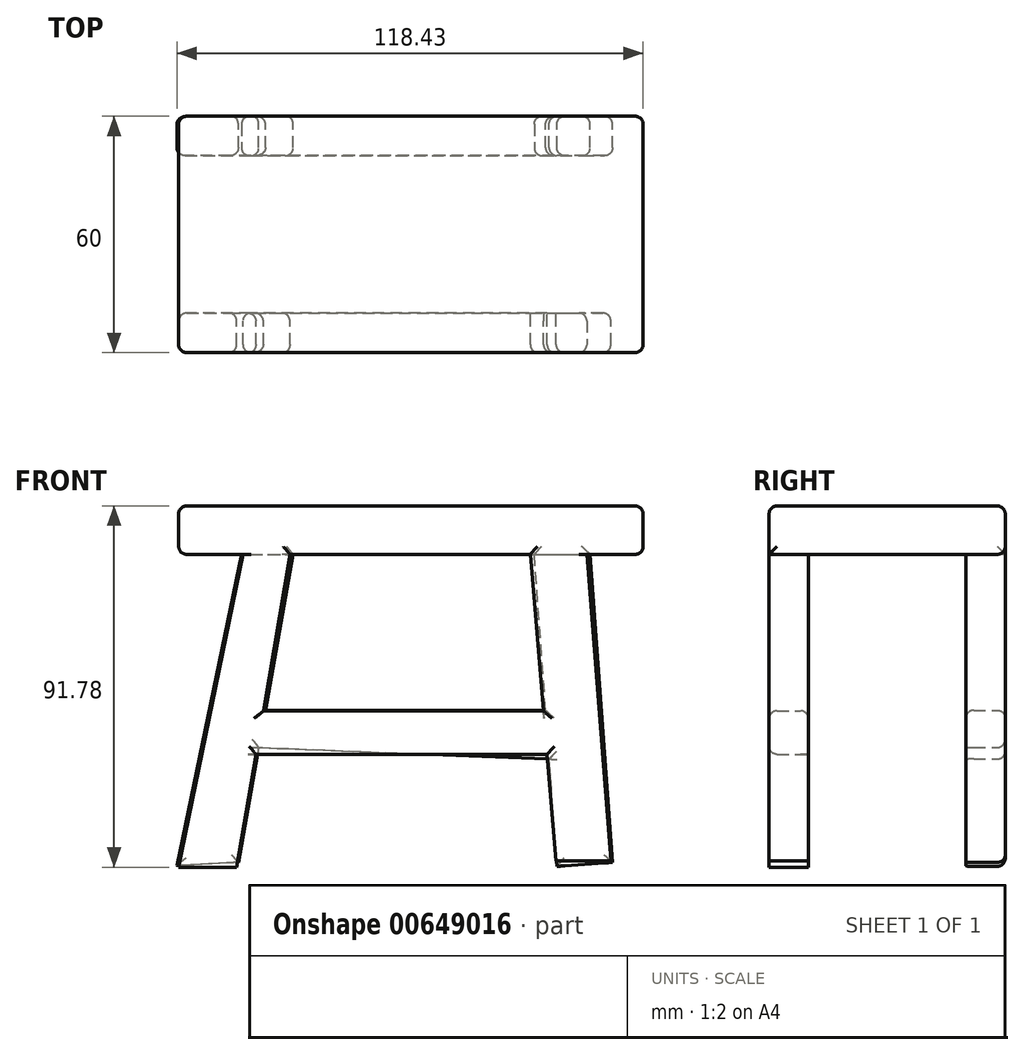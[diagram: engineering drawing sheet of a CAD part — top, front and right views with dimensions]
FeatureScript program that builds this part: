
annotation { "Feature Type Name" : "Feature", "Feature Type Description" : "" }
export const myFeature = defineFeature(function(context is Context, id is Id, definition is map)
    precondition{}
    {
        {
            var Q0;
            Q0=qCreatedBy(makeId("Front.planeOp"),FACE);
            var sketch = newSketch(context, id + "F0", { "sketchPlane" : qUnion([Q0])});
            skLineSegment(sketch, "E0.bottom", {"start": v(-57.16, 35.65) * mm, "end": v(60.84, 35.65) * mm});
            skLineSegment(sketch, "E0.top", {"start": v(-57.16, 23.35) * mm, "end": v(60.84, 23.35) * mm});
            skLineSegment(sketch, "E0.left", {"start": v(-57.16, 35.65) * mm, "end": v(-57.16, 23.35) * mm});
            skLineSegment(sketch, "E0.right", {"start": v(60.84, 35.65) * mm, "end": v(60.84, 23.35) * mm});
            skSolve(sketch);
        }
        {
            var Q0;
            Q0 = qSketchRegion(id + "F0", true);
            extrude(context, id + "F1", {"entities" : qUnion([Q0]), "depth" : 60 * mm, "offsetDistance" : 25 * mm});
        }
        {
            var Q0;
            Q0=qCreatedBy(makeId("Front.planeOp"),FACE);
            cPlane(context, id + "F2", {"entities" : qUnion([Q0]), "cplaneType" : CPlaneType.OFFSET, "offset" : 50 * mm, "width" : 150 * mm, "height" : 150 * mm});
        }
        {
            var Q0;
            Q0=qCreatedBy(id+"F2.planeOp",FACE);
            var sketch = newSketch(context, id + "F3", { "sketchPlane" : qUnion([Q0])});
            skLineSegment(sketch, "E1", {"start": v(-40.77, 23.76) * mm, "end": v(-57.16, -56.13) * mm});
            skLineSegment(sketch, "E2", {"start": v(-57.16, -56.13) * mm, "end": v(-42.4, -56.13) * mm});
            skLineSegment(sketch, "E3", {"start": v(-42.4, -56.13) * mm, "end": v(-28.88, 23.35) * mm});
            skLineSegment(sketch, "E4", {"start": v(-28.88, 23.35) * mm, "end": v(-40.77, 23.76) * mm});
            skLineSegment(sketch, "E5", {"start": v(32.16, 23.35) * mm, "end": v(38.72, -54.5) * mm});
            skLineSegment(sketch, "E6", {"start": v(38.72, -54.5) * mm, "end": v(52.65, -54.5) * mm});
            skLineSegment(sketch, "E7", {"start": v(52.65, -54.5) * mm, "end": v(46.5, 23.76) * mm});
            skLineSegment(sketch, "E8", {"start": v(46.5, 23.76) * mm, "end": v(32.16, 23.35) * mm});
            skLineSegment(sketch, "E9", {"start": v(-35.65, -16.39) * mm, "end": v(35.5, -16.39) * mm});
            skLineSegment(sketch, "E10", {"start": v(35.5, -16.39) * mm, "end": v(36.44, -27.45) * mm});
            skLineSegment(sketch, "E11", {"start": v(36.44, -27.45) * mm, "end": v(-37.53, -27.45) * mm});
            skLineSegment(sketch, "E12", {"start": v(-37.53, -27.45) * mm, "end": v(-35.65, -16.39) * mm});
            skSolve(sketch);
        }
        {
            var Q0;
            Q0 = qSketchRegion(id + "F3", true);
            extrude(context, id + "F4", {"entities" : qUnion([Q0]), "operationType" : NewBodyOperationType.ADD, "depth" : 10 * mm, "offsetDistance" : 25 * mm});
        }
        {
            var Q0;
            Q0=qCreatedBy(makeId("Front.planeOp"),FACE);
            var sketch = newSketch(context, id + "F5", { "sketchPlane" : qUnion([Q0])});
            skLineSegment(sketch, "E13", {"start": v(47.32, 24.17) * mm, "end": v(53.06, -54.9) * mm});
            skLineSegment(sketch, "E14", {"start": v(53.06, -54.9) * mm, "end": v(38.94, -55.93) * mm});
            skLineSegment(sketch, "E15", {"start": v(38.94, -55.93) * mm, "end": v(33.18, 23.43) * mm});
            skLineSegment(sketch, "E16", {"start": v(33.18, 23.43) * mm, "end": v(47.32, 24.17) * mm});
            skLineSegment(sketch, "E17", {"start": v(-28.07, 23.43) * mm, "end": v(-42, -54.9) * mm});
            skLineSegment(sketch, "E18", {"start": v(-42, -54.9) * mm, "end": v(-57.59, -55.72) * mm});
            skLineSegment(sketch, "E19", {"start": v(-57.59, -55.72) * mm, "end": v(-41.18, 23.43) * mm});
            skLineSegment(sketch, "E20", {"start": v(-41.18, 23.43) * mm, "end": v(-28.07, 23.43) * mm});
            skLineSegment(sketch, "E21", {"start": v(36.06, -16.25) * mm, "end": v(-35.12, -16.25) * mm});
            skLineSegment(sketch, "E22", {"start": v(-35.12, -16.25) * mm, "end": v(-36.8, -25.72) * mm});
            skLineSegment(sketch, "E23", {"start": v(36.75, -25.72) * mm, "end": v(36.06, -16.25) * mm});
            skLineSegment(sketch, "E24", {"start": v(-36.8, -25.72) * mm, "end": v(36.96, -28.66) * mm});
            skSolve(sketch);
        }
        {
            var Q0;
            Q0 = qSketchRegion(id + "F5", true);
            extrude(context, id + "F6", {"entities" : qUnion([Q0]), "operationType" : NewBodyOperationType.ADD, "depth" : 10 * mm, "offsetDistance" : 25 * mm});
        }
        {
            var Q0;
            Q0=qCreatedBy(makeId("Right.planeOp"),FACE);
            var sketch = newSketch(context, id + "F7", { "sketchPlane" : qUnion([Q0])});
            skLineSegment(sketch, "E25.bottom", {"start": v(-49.78, 23.35) * mm, "end": v(-10.45, 23.35) * mm});
            skLineSegment(sketch, "E25.top", {"start": v(-49.78, -67.6) * mm, "end": v(-10.45, -67.6) * mm});
            skLineSegment(sketch, "E25.left", {"start": v(-49.78, 23.35) * mm, "end": v(-49.78, -67.6) * mm});
            skLineSegment(sketch, "E25.right", {"start": v(-10.45, 23.35) * mm, "end": v(-10.45, -67.6) * mm});
            skSolve(sketch);
        }
        {
            var Q0;
            Q0 = qSketchRegion(id + "F7", true);
            extrude(context, id + "F8", {"entities" : qUnion([Q0]), "operationType" : NewBodyOperationType.REMOVE, "endBound" : BoundingType.THROUGH_ALL, "oppositeDirection" : true, "depth" : 100 * mm, "offsetDistance" : 25 * mm, "hasSecondDirection" : true, "secondDirectionOppositeDirection" : false, "secondDirectionDepth" : 100 * mm});
        }
        {
            var Q0;
            Q0=makeQuery(id+"F1.opExtrude","CAP_EDGE",EDGE,{"disambiguationData":[OSD([sQuery(id+"F0.wireOp",EDGE,"E0.bottom")])],"isStart":false});
            var Q1;
            {var subQ0=sQuery(id+"F3.wireOp",EDGE,"E4");var subQ1=sQuery(id+"F3.wireOp",EDGE,"E3");var subQ5=sQuery(id+"F0.wireOp",EDGE,"E0.top");Q1=makeQuery(id+"F4.boolean.opBoolean","SPLIT",EDGE,{"disambiguationData":[TD([makeQuery(id+"F4.opExtrude","SWEPT_FACE",FACE,{"disambiguationData":[OSD([subQ1]),TDD([makeQuery(id+"F3.imprint","IMPRINT",EDGE,{"disambiguationData":[TD([[makeQuery(id+"F3.imprint","INTERSECT",VERTEX,{"derivedFrom":[subQ1,subQ0]}),1.0]])],"derivedFrom":subQ1})])]})])],"derivedFrom":makeQuery(id+"F1.opExtrude","CAP_EDGE",EDGE,{"disambiguationData":[OSD([subQ5])],"isStart":false})});}
            var Q2;
            {var subQ0=sQuery(id+"F3.wireOp",EDGE,"E3");Q2=makeQuery(id+"F4.opExtrude","CAP_EDGE",EDGE,{"disambiguationData":[OSD([subQ0]),TDD([makeQuery(id+"F3.imprint","IMPRINT",EDGE,{"disambiguationData":[TD([[makeQuery(id+"F3.imprint","INTERSECT",VERTEX,{"derivedFrom":[subQ0,sQuery(id+"F3.wireOp",EDGE,"E4")]}),1.0]])],"derivedFrom":subQ0})])],"isStart":false});}
            var Q3;
            {var subQ0=sQuery(id+"F3.wireOp",EDGE,"E5");Q3=makeQuery(id+"F4.opExtrude","CAP_EDGE",EDGE,{"disambiguationData":[OSD([subQ0]),TDD([makeQuery(id+"F3.imprint","IMPRINT",EDGE,{"disambiguationData":[TD([[makeQuery(id+"F3.imprint","INTERSECT",VERTEX,{"derivedFrom":[subQ0,sQuery(id+"F3.wireOp",EDGE,"E8")]}),-1.0]])],"derivedFrom":subQ0})])],"isStart":false});}
            var Q4;
            Q4=makeQuery(id+"F4.opExtrude","CAP_EDGE",EDGE,{"disambiguationData":[OSD([sQuery(id+"F3.wireOp",EDGE,"E9")])],"isStart":false});
            var Q5;
            Q5=makeQuery(id+"F4.opExtrude","CAP_EDGE",EDGE,{"disambiguationData":[OSD([sQuery(id+"F3.wireOp",EDGE,"E11")])],"isStart":false});
            var Q6;
            {var subQ0=sQuery(id+"F3.wireOp",EDGE,"E5");Q6=makeQuery(id+"F4.opExtrude","CAP_EDGE",EDGE,{"disambiguationData":[OSD([subQ0]),TDD([makeQuery(id+"F3.imprint","IMPRINT",EDGE,{"disambiguationData":[TD([[makeQuery(id+"F3.imprint","INTERSECT",VERTEX,{"derivedFrom":[subQ0,sQuery(id+"F3.wireOp",EDGE,"E6")]}),1.0]])],"derivedFrom":subQ0})])],"isStart":false});}
            var Q7;
            Q7=makeQuery(id+"F4.opExtrude","CAP_EDGE",EDGE,{"disambiguationData":[OSD([sQuery(id+"F3.wireOp",EDGE,"E7")])],"isStart":false});
            var Q8;
            Q8=makeQuery(id+"F4.opExtrude","CAP_EDGE",EDGE,{"disambiguationData":[OSD([sQuery(id+"F3.wireOp",EDGE,"E7")])],"isStart":true});
            var Q9;
            Q9=makeQuery(id+"F1.opExtrude","SWEPT_EDGE",EDGE,{"disambiguationData":[OSD([sQuery(id+"F0.wireOp",EDGE,"E0.top"),sQuery(id+"F0.wireOp",EDGE,"E0.right")])]});
            var Q10;
            Q10=makeQuery(id+"F1.opExtrude","SWEPT_EDGE",EDGE,{"disambiguationData":[OSD([sQuery(id+"F0.wireOp",EDGE,"E0.bottom"),sQuery(id+"F0.wireOp",EDGE,"E0.right")])]});
            var Q11;
            Q11=makeQuery(id+"F1.opExtrude","CAP_EDGE",EDGE,{"disambiguationData":[OSD([sQuery(id+"F0.wireOp",EDGE,"E0.bottom")])],"isStart":true});
            var Q12;
            {var subQ3=sQuery(id+"F5.wireOp",EDGE,"E16");var subQ4=sQuery(id+"F5.wireOp",EDGE,"E15");var subQ5=sQuery(id+"F0.wireOp",EDGE,"E0.top");Q12=makeQuery(id+"F6.boolean.opBoolean","SPLIT",EDGE,{"disambiguationData":[TD([makeQuery(id+"F6.opExtrude","SWEPT_FACE",FACE,{"disambiguationData":[OSD([subQ4]),TDD([makeQuery(id+"F5.imprint","IMPRINT",EDGE,{"disambiguationData":[TD([[makeQuery(id+"F5.imprint","INTERSECT",VERTEX,{"derivedFrom":[subQ4,subQ3]}),1.0]])],"derivedFrom":subQ4})])]})])],"derivedFrom":makeQuery(id+"F1.opExtrude","CAP_EDGE",EDGE,{"disambiguationData":[OSD([subQ5])],"isStart":true})});}
            var Q13;
            {var subQ0=sQuery(id+"F0.wireOp",EDGE,"E0.right");var subQ2=sQuery(id+"F0.wireOp",EDGE,"E0.top");Q13=makeQuery(id+"F6.boolean.opBoolean","SPLIT",EDGE,{"disambiguationData":[TD([makeQuery(id+"F1.opExtrude","SWEPT_FACE",FACE,{"disambiguationData":[OSD([subQ0])]})])],"derivedFrom":makeQuery(id+"F1.opExtrude","CAP_EDGE",EDGE,{"disambiguationData":[OSD([subQ2])],"isStart":true})});}
            var Q14;
            Q14=makeQuery(id+"F1.opExtrude","SWEPT_EDGE",EDGE,{"disambiguationData":[OSD([sQuery(id+"F0.wireOp",EDGE,"E0.bottom"),sQuery(id+"F0.wireOp",EDGE,"E0.left")])]});
            var Q15;
            Q15=makeQuery(id+"F1.opExtrude","SWEPT_EDGE",EDGE,{"disambiguationData":[OSD([sQuery(id+"F0.wireOp",EDGE,"E0.top"),sQuery(id+"F0.wireOp",EDGE,"E0.left")])]});
            var Q16;
            Q16=makeQuery(id+"F1.opExtrude","CAP_EDGE",EDGE,{"disambiguationData":[OSD([sQuery(id+"F0.wireOp",EDGE,"E0.left")])],"isStart":false});
            var Q17;
            Q17=makeQuery(id+"F1.opExtrude","CAP_EDGE",EDGE,{"disambiguationData":[OSD([sQuery(id+"F0.wireOp",EDGE,"E0.left")])],"isStart":true});
            var Q18;
            Q18=makeQuery(id+"F1.opExtrude","CAP_EDGE",EDGE,{"disambiguationData":[OSD([sQuery(id+"F0.wireOp",EDGE,"E0.right")])],"isStart":true});
            var Q19;
            Q19=makeQuery(id+"F1.opExtrude","CAP_EDGE",EDGE,{"disambiguationData":[OSD([sQuery(id+"F0.wireOp",EDGE,"E0.right")])],"isStart":false});
            var Q20;
            Q20=makeQuery(id+"F6.opExtrude","CAP_EDGE",EDGE,{"disambiguationData":[OSD([sQuery(id+"F5.wireOp",EDGE,"E13")])],"isStart":true});
            var Q21;
            Q21=makeQuery(id+"F6.opExtrude","CAP_EDGE",EDGE,{"disambiguationData":[OSD([sQuery(id+"F5.wireOp",EDGE,"E19")])],"isStart":true});
            var Q22;
            Q22=makeQuery(id+"F4.opExtrude","CAP_EDGE",EDGE,{"disambiguationData":[OSD([sQuery(id+"F3.wireOp",EDGE,"E1")])],"isStart":true});
            var Q23;
            {var subQ0=sQuery(id+"F5.wireOp",EDGE,"E17");Q23=makeQuery(id+"F6.opExtrude","CAP_EDGE",EDGE,{"disambiguationData":[OSD([subQ0]),TDD([makeQuery(id+"F5.imprint","IMPRINT",EDGE,{"disambiguationData":[TD([[makeQuery(id+"F5.imprint","INTERSECT",VERTEX,{"derivedFrom":[subQ0,sQuery(id+"F5.wireOp",EDGE,"E18")]}),1.0]])],"derivedFrom":subQ0})])],"isStart":true});}
            var Q24;
            Q24=makeQuery(id+"F6.opExtrude","CAP_EDGE",EDGE,{"disambiguationData":[OSD([sQuery(id+"F5.wireOp",EDGE,"E18")])],"isStart":true});
            var Q25;
            Q25=makeQuery(id+"F6.opExtrude","CAP_EDGE",EDGE,{"disambiguationData":[OSD([sQuery(id+"F5.wireOp",EDGE,"E24")])],"isStart":true});
            var Q26;
            {var subQ0=sQuery(id+"F5.wireOp",EDGE,"E15");Q26=makeQuery(id+"F6.opExtrude","CAP_EDGE",EDGE,{"disambiguationData":[OSD([subQ0]),TDD([makeQuery(id+"F5.imprint","IMPRINT",EDGE,{"disambiguationData":[TD([[makeQuery(id+"F5.imprint","INTERSECT",VERTEX,{"derivedFrom":[sQuery(id+"F5.wireOp",EDGE,"E14"),subQ0]}),-1.0]])],"derivedFrom":subQ0})])],"isStart":true});}
            var Q27;
            Q27=makeQuery(id+"F6.opExtrude","CAP_EDGE",EDGE,{"disambiguationData":[OSD([sQuery(id+"F5.wireOp",EDGE,"E14")])],"isStart":true});
            var Q28;
            {var subQ0=sQuery(id+"F5.wireOp",EDGE,"E15");Q28=makeQuery(id+"F6.opExtrude","CAP_EDGE",EDGE,{"disambiguationData":[OSD([subQ0]),TDD([makeQuery(id+"F5.imprint","IMPRINT",EDGE,{"disambiguationData":[TD([[makeQuery(id+"F5.imprint","INTERSECT",VERTEX,{"derivedFrom":[subQ0,sQuery(id+"F5.wireOp",EDGE,"E16")]}),1.0]])],"derivedFrom":subQ0})])],"isStart":true});}
            var Q29;
            Q29=makeQuery(id+"F6.opExtrude","CAP_EDGE",EDGE,{"disambiguationData":[OSD([sQuery(id+"F5.wireOp",EDGE,"E21")])],"isStart":true});
            var Q30;
            {var subQ0=sQuery(id+"F5.wireOp",EDGE,"E17");Q30=makeQuery(id+"F6.opExtrude","CAP_EDGE",EDGE,{"disambiguationData":[OSD([subQ0]),TDD([makeQuery(id+"F5.imprint","IMPRINT",EDGE,{"disambiguationData":[TD([[makeQuery(id+"F5.imprint","INTERSECT",VERTEX,{"derivedFrom":[subQ0,sQuery(id+"F5.wireOp",EDGE,"E20")]}),-1.0]])],"derivedFrom":subQ0})])],"isStart":true});}
            var Q31;
            {var subQ0=sQuery(id+"F5.wireOp",EDGE,"E17");Q31=makeQuery(id+"F6.opExtrude","CAP_EDGE",EDGE,{"disambiguationData":[OSD([subQ0]),TDD([makeQuery(id+"F5.imprint","IMPRINT",EDGE,{"disambiguationData":[TD([[makeQuery(id+"F5.imprint","INTERSECT",VERTEX,{"derivedFrom":[subQ0,sQuery(id+"F5.wireOp",EDGE,"E20")]}),-1.0]])],"derivedFrom":subQ0})])],"isStart":false});}
            var Q32;
            {var subQ0=sQuery(id+"F5.wireOp",EDGE,"E17");Q32=makeQuery(id+"F6.opExtrude","CAP_EDGE",EDGE,{"disambiguationData":[OSD([subQ0]),TDD([makeQuery(id+"F5.imprint","IMPRINT",EDGE,{"disambiguationData":[TD([[makeQuery(id+"F5.imprint","INTERSECT",VERTEX,{"derivedFrom":[subQ0,sQuery(id+"F5.wireOp",EDGE,"E18")]}),1.0]])],"derivedFrom":subQ0})])],"isStart":false});}
            var Q33;
            {var subQ0=sQuery(id+"F3.wireOp",EDGE,"E3");Q33=makeQuery(id+"F4.opExtrude","CAP_EDGE",EDGE,{"disambiguationData":[OSD([subQ0]),TDD([makeQuery(id+"F3.imprint","IMPRINT",EDGE,{"disambiguationData":[TD([[makeQuery(id+"F3.imprint","INTERSECT",VERTEX,{"derivedFrom":[sQuery(id+"F3.wireOp",EDGE,"E2"),subQ0]}),-1.0]])],"derivedFrom":subQ0})])],"isStart":false});}
            var Q34;
            {var subQ0=sQuery(id+"F5.wireOp",EDGE,"E15");Q34=makeQuery(id+"F6.opExtrude","CAP_EDGE",EDGE,{"disambiguationData":[OSD([subQ0]),TDD([makeQuery(id+"F5.imprint","IMPRINT",EDGE,{"disambiguationData":[TD([[makeQuery(id+"F5.imprint","INTERSECT",VERTEX,{"derivedFrom":[subQ0,sQuery(id+"F5.wireOp",EDGE,"E16")]}),1.0]])],"derivedFrom":subQ0})])],"isStart":false});}
            var Q35;
            Q35=makeQuery(id+"F6.opExtrude","CAP_EDGE",EDGE,{"disambiguationData":[OSD([sQuery(id+"F5.wireOp",EDGE,"E13")])],"isStart":false});
            var Q36;
            Q36=makeQuery(id+"F4.opExtrude","CAP_EDGE",EDGE,{"disambiguationData":[OSD([sQuery(id+"F3.wireOp",EDGE,"E1")])],"isStart":false});
            var Q37;
            Q37=makeQuery(id+"F6.opExtrude","CAP_EDGE",EDGE,{"disambiguationData":[OSD([sQuery(id+"F5.wireOp",EDGE,"E21")])],"isStart":false});
            var Q38;
            Q38=makeQuery(id+"F4.opExtrude","CAP_EDGE",EDGE,{"disambiguationData":[OSD([sQuery(id+"F3.wireOp",EDGE,"E9")])],"isStart":true});
            var Q39;
            {var subQ0=sQuery(id+"F3.wireOp",EDGE,"E3");Q39=makeQuery(id+"F4.opExtrude","CAP_EDGE",EDGE,{"disambiguationData":[OSD([subQ0]),TDD([makeQuery(id+"F3.imprint","IMPRINT",EDGE,{"disambiguationData":[TD([[makeQuery(id+"F3.imprint","INTERSECT",VERTEX,{"derivedFrom":[subQ0,sQuery(id+"F3.wireOp",EDGE,"E4")]}),1.0]])],"derivedFrom":subQ0})])],"isStart":true});}
            var Q40;
            Q40=makeQuery(id+"F6.opExtrude","CAP_EDGE",EDGE,{"disambiguationData":[OSD([sQuery(id+"F5.wireOp",EDGE,"E19")])],"isStart":false});
            var Q41;
            {var subQ0=sQuery(id+"F3.wireOp",EDGE,"E3");Q41=makeQuery(id+"F4.opExtrude","CAP_EDGE",EDGE,{"disambiguationData":[OSD([subQ0]),TDD([makeQuery(id+"F3.imprint","IMPRINT",EDGE,{"disambiguationData":[TD([[makeQuery(id+"F3.imprint","INTERSECT",VERTEX,{"derivedFrom":[sQuery(id+"F3.wireOp",EDGE,"E2"),subQ0]}),-1.0]])],"derivedFrom":subQ0})])],"isStart":true});}
            var Q42;
            {var subQ0=sQuery(id+"F5.wireOp",EDGE,"E15");Q42=makeQuery(id+"F6.opExtrude","CAP_EDGE",EDGE,{"disambiguationData":[OSD([subQ0]),TDD([makeQuery(id+"F5.imprint","IMPRINT",EDGE,{"disambiguationData":[TD([[makeQuery(id+"F5.imprint","INTERSECT",VERTEX,{"derivedFrom":[sQuery(id+"F5.wireOp",EDGE,"E14"),subQ0]}),-1.0]])],"derivedFrom":subQ0})])],"isStart":false});}
            fillet(context, id + "F9", {"entities" : qUnion([Q0, Q1, Q2, Q3, Q4, Q5, Q6, Q7, Q8, Q9, Q10, Q11, Q12, Q13, Q14, Q15, Q16, Q17, Q18, Q19, Q20, Q21, Q22, Q23, Q24, Q25, Q26, Q27, Q28, Q29, Q30, Q31, Q32, Q33, Q34, Q35, Q36, Q37, Q38, Q39, Q40, Q41, Q42]), "radius" : 2 * mm, "tangentPropagation" : true, "allowEdgeOverflow" : false});
        }
    });
